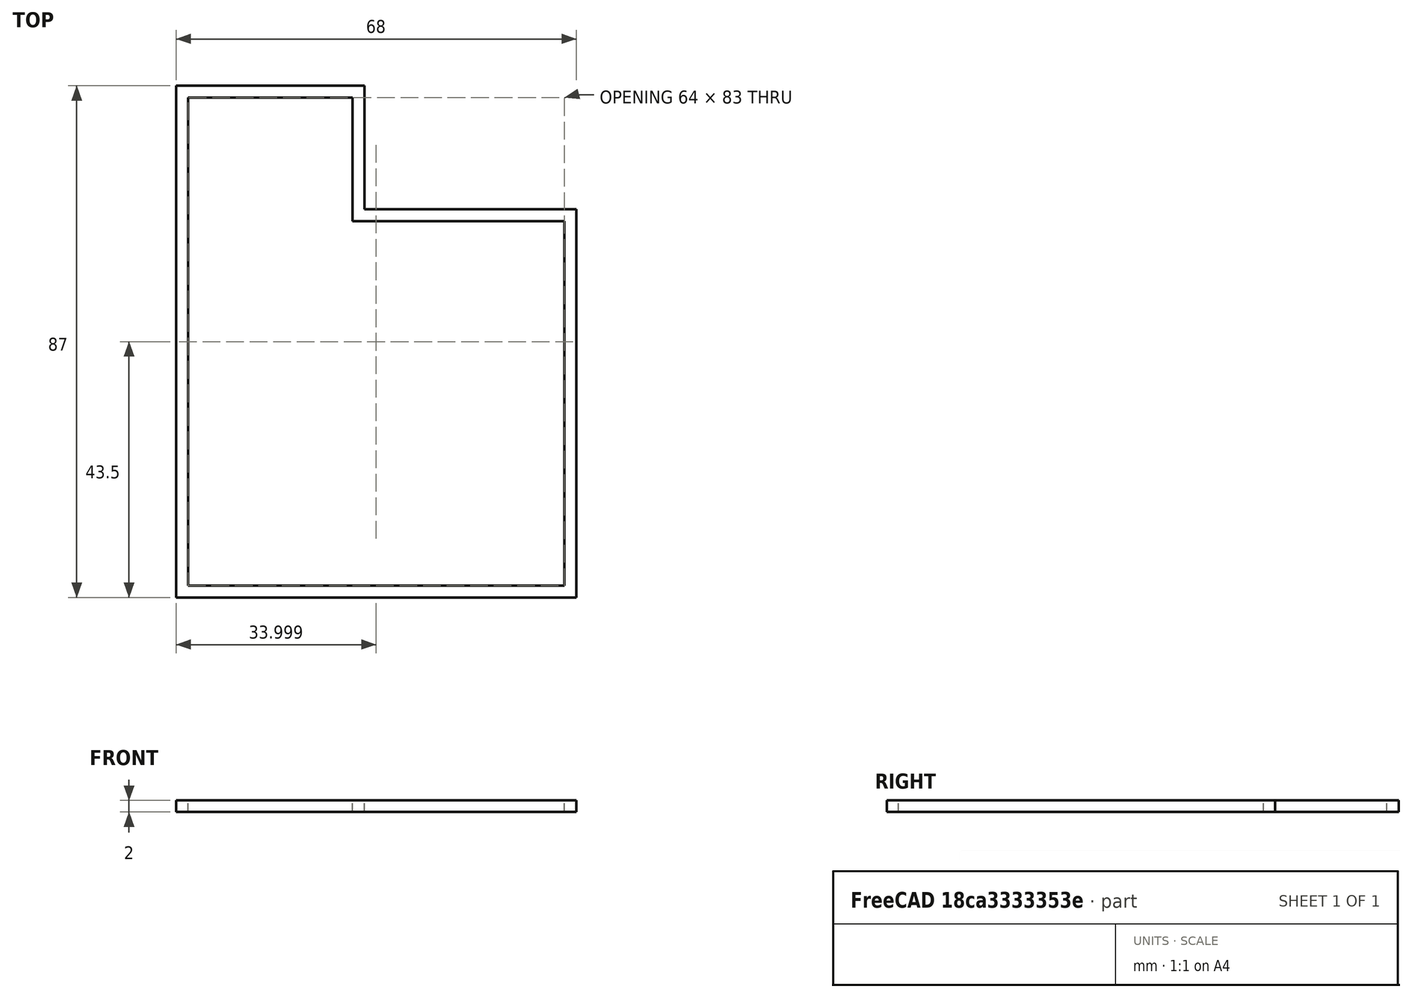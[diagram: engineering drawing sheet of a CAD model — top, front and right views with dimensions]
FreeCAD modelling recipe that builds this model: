
FCSTD DOCUMENT  (FreeCAD 0.19R24366 (Git))
Label: holder
License: All rights reserved
LicenseURL: http://en.wikipedia.org/wiki/All_rights_reserved
objects: Sketcher::SketchObject×1, PartDesign::Pad×1, PartDesign::Body×1
note: 4 computed .brp shape members not serialized (recipe doc carries the construction recipe); baked Part::Feature solids carry a one-line shape summary decoded from their .brp

FEATURE [Sketcher::SketchObject] Sketch
  FullyConstrained = false
  MapMode = 5
  Support = -> [XY_Plane]
  sketch-geometry (12):
    g0: LineSegment StartX=-39.2006 StartY=83 StartZ=0 EndX=-39.2006 EndY=0 EndZ=0
    g1: LineSegment StartX=-39.2006 StartY=0 StartZ=0 EndX=24.7994 EndY=0 EndZ=0
    g2: LineSegment StartX=24.7994 StartY=0 StartZ=0 EndX=24.7994 EndY=62 EndZ=0
    g3: LineSegment StartX=24.7994 StartY=62 StartZ=0 EndX=-11.2006 EndY=62 EndZ=0
    g4: LineSegment StartX=-11.2006 StartY=62 StartZ=0 EndX=-11.2006 EndY=83 EndZ=0
    g5: LineSegment StartX=-11.2006 StartY=83 StartZ=0 EndX=-39.2006 EndY=83 EndZ=0
    g6: LineSegment StartX=-41.2006 StartY=85 StartZ=0 EndX=-41.2006 EndY=-2 EndZ=0
    g7: LineSegment StartX=-41.2006 StartY=-2 StartZ=0 EndX=26.7994 EndY=-2 EndZ=0
    g8: LineSegment StartX=26.7994 StartY=-2 StartZ=0 EndX=26.7994 EndY=64 EndZ=0
    g9: LineSegment StartX=26.7994 StartY=64 StartZ=0 EndX=-9.20056 EndY=64 EndZ=0
    g10: LineSegment StartX=-9.20056 StartY=64 StartZ=0 EndX=-9.20056 EndY=85 EndZ=0
    g11: LineSegment StartX=-9.20056 StartY=85 StartZ=0 EndX=-41.2006 EndY=85 EndZ=0
  constraints (35):
    c: PointOnObject(g0,g-1)
    c: Vertical(g0)
    c: Coincident(g0,g1)
    c: PointOnObject(g1,g-1)
    c: Coincident(g1,g2)
    c: Vertical(g2)
    c: Coincident(g2,g3)
    c: Horizontal(g3)
    c: Coincident(g3,g4)
    c: Vertical(g4)
    c: Coincident(g4,g5)
    c: Horizontal(g5)
    c: DistanceX(g1,g1) = 64
    c: DistanceY(g2,g2) = 62
    c: DistanceX(g3,g3) = 36
    c: DistanceY(g4,g4) = 21
    c: Coincident(g0,g5)
    c: Vertical(g6)
    c: Coincident(g6,g7)
    c: Horizontal(g7)
    c: Coincident(g7,g8)
    c: Vertical(g8)
    c: Coincident(g8,g9)
    c: Horizontal(g9)
    c: Coincident(g9,g10)
    c: Vertical(g10)
    c: Coincident(g10,g11)
    c: Coincident(g11,g6)
    c: DistanceX(g6,g0) = 2
    c: DistanceY(g6,g0) = 2
    c: DistanceX(g1,g7) = 2
    c: DistanceY(g0,g6) = 2
    c: DistanceY(g4,g10) = 2
    c: DistanceX(g3,g9) = 2
    c: DistanceY(g3,g9) = 2
FEATURE [PartDesign::Pad] Pad
  Direction = (1,1,1)
  Length = 2
  Length2 = 100
  Profile = -> Sketch
  Type = 0
FEATURE [PartDesign::Body] Body
  Group = -> [Sketch,Pad]
  Origin = -> Origin
  Tip = -> Pad
